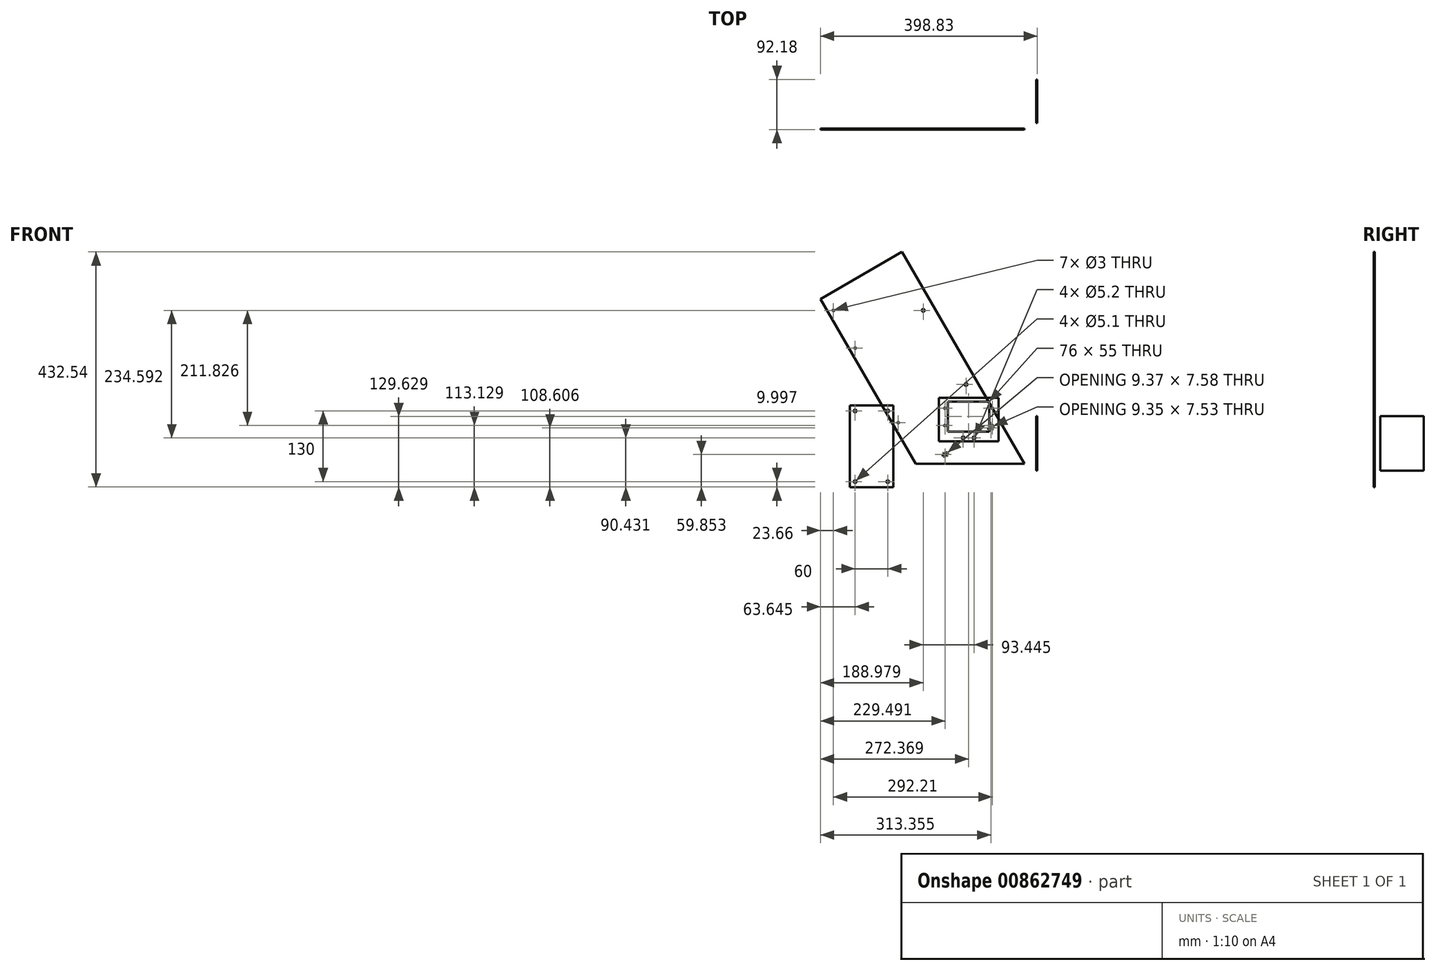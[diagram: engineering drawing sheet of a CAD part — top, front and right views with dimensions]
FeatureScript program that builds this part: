
annotation { "Feature Type Name" : "Feature", "Feature Type Description" : "" }
export const myFeature = defineFeature(function(context is Context, id is Id, definition is map)
    precondition{}
    {
        {
            var Q0;
            Q0=qCreatedBy(makeId("Front.planeOp"),FACE);
            var sketch = newSketch(context, id + "F0", { "sketchPlane" : qUnion([Q0])});
            skLineSegment(sketch, "E0", {"start": v(-221.83, -33.9) * mm, "end": v(-21.83, -33.9) * mm});
            skLineSegment(sketch, "E1", {"start": v(-21.83, -33.9) * mm, "end": v(-71.83, 52.7) * mm});
            skLineSegment(sketch, "E2", {"start": v(-71.83, 52.7) * mm, "end": v(-221.83, -33.9) * mm, "construction": true});
            skPoint(sketch, "E3", {"position": v(-150.09, -27.11) * mm});
            skLineSegment(sketch, "E4.bottom", {"start": v(-163.9, -17.83) * mm, "end": v(-168.23, -20.33) * mm});
            skLineSegment(sketch, "E4.top", {"start": v(-166.45, -13.4) * mm, "end": v(-170.78, -15.9) * mm});
            skLineSegment(sketch, "E4.left", {"start": v(-162.98, -14.41) * mm, "end": v(-163.03, -14.32) * mm});
            skLineSegment(sketch, "E4.right", {"start": v(-171.64, -19.41) * mm, "end": v(-171.7, -19.32) * mm});
            skPoint(sketch, "E4.middle", {"position": v(-167.34, -16.87) * mm});
            skPoint(sketch, "E5.visualSharp", {"position": v(-164.28, -12.16) * mm});
            skArc(sketch, "E5.filletArc", {"start": v(-163.03, -14.32) * mm, "mid": v(-164.55, -13.16) * mm, "end": v(-166.45, -13.4) * mm});
            skPoint(sketch, "E6.visualSharp", {"position": v(-161.73, -16.58) * mm});
            skArc(sketch, "E6.filletArc", {"start": v(-163.9, -17.83) * mm, "mid": v(-162.73, -16.3) * mm, "end": v(-162.98, -14.41) * mm});
            skPoint(sketch, "E7.visualSharp", {"position": v(-170.4, -21.58) * mm});
            skArc(sketch, "E7.filletArc", {"start": v(-171.64, -19.41) * mm, "mid": v(-170.13, -20.57) * mm, "end": v(-168.23, -20.33) * mm});
            skPoint(sketch, "E8.visualSharp", {"position": v(-172.94, -17.16) * mm});
            skArc(sketch, "E8.filletArc", {"start": v(-170.78, -15.9) * mm, "mid": v(-171.94, -17.43) * mm, "end": v(-171.7, -19.32) * mm});
            skLineSegment(sketch, "E9.bottom", {"start": v(-80.04, 30.95) * mm, "end": v(-84.38, 28.45) * mm});
            skLineSegment(sketch, "E9.top", {"start": v(-82.57, 35.33) * mm, "end": v(-86.9, 32.82) * mm});
            skLineSegment(sketch, "E9.left", {"start": v(-79.03, 34.17) * mm, "end": v(-79.05, 34.22) * mm});
            skLineSegment(sketch, "E9.right", {"start": v(-87.9, 29.56) * mm, "end": v(-87.92, 29.6) * mm});
            skPoint(sketch, "E9.middle", {"position": v(-82.9, 31.88) * mm});
            skArc(sketch, "E10.filletArc", {"start": v(-79.05, 34.22) * mm, "mid": v(-80.56, 35.55) * mm, "end": v(-82.57, 35.33) * mm});
            skArc(sketch, "E11.filletArc", {"start": v(-80.04, 30.95) * mm, "mid": v(-78.91, 32.36) * mm, "end": v(-79.03, 34.17) * mm});
            skArc(sketch, "E12.filletArc", {"start": v(-87.9, 29.56) * mm, "mid": v(-86.39, 28.23) * mm, "end": v(-84.38, 28.45) * mm});
            skArc(sketch, "E13.filletArc", {"start": v(-86.9, 32.82) * mm, "mid": v(-88.04, 31.4) * mm, "end": v(-87.92, 29.6) * mm});
            skLineSegment(sketch, "E14", {"start": v(-221.83, -33.9) * mm, "end": v(-396.83, 269.21) * mm});
            skLineSegment(sketch, "E15", {"start": v(-396.83, 269.21) * mm, "end": v(-246.83, 355.82) * mm});
            skLineSegment(sketch, "E16", {"start": v(-246.83, 355.82) * mm, "end": v(-71.83, 52.7) * mm});
            skCircle(sketch, "E17", {"center": v(-129.15, 112) * mm, "radius": 2.6 * mm});
            skCircle(sketch, "E18", {"center": v(-207.85, 248.3) * mm, "radius": 2.6 * mm});
            skCircle(sketch, "E19", {"center": v(-253.92, 41.69) * mm, "radius": 1.5 * mm});
            skCircle(sketch, "E20", {"center": v(-333.17, 178.95) * mm, "radius": 1.5 * mm});
            skCircle(sketch, "E21", {"center": v(-373.17, 248.23) * mm, "radius": 1.5 * mm});
            skSolve(sketch);
        }
        {
            var Q0;
            Q0 = qSketchRegion(id + "F0", true);
            extrude(context, id + "F1", {"entities" : qUnion([Q0]), "depth" : 2 * mm, "offsetDistance" : 25 * mm});
        }
        {
            var Q0;
            Q0=qCreatedBy(makeId("Right.planeOp"),FACE);
            var sketch = newSketch(context, id + "F2", { "sketchPlane" : qUnion([Q0])});
            skLineSegment(sketch, "E22.bottom", {"start": v(10.18, 53.74) * mm, "end": v(90.18, 53.74) * mm});
            skLineSegment(sketch, "E22.top", {"start": v(10.18, -46.26) * mm, "end": v(90.18, -46.26) * mm});
            skLineSegment(sketch, "E22.left", {"start": v(10.18, 53.74) * mm, "end": v(10.18, -46.26) * mm});
            skLineSegment(sketch, "E22.right", {"start": v(90.18, 53.74) * mm, "end": v(90.18, -46.26) * mm});
            skSolve(sketch);
        }
        {
            var Q0;
            Q0 = qSketchRegion(id + "F2", true);
            extrude(context, id + "F3", {"entities" : qUnion([Q0]), "depth" : 2 * mm, "offsetDistance" : 25 * mm});
        }
        {
            var Q0;
            Q0=qCreatedBy(makeId("Front.planeOp"),FACE);
            var sketch = newSketch(context, id + "F4", { "sketchPlane" : qUnion([Q0])});
            skLineSegment(sketch, "E23.bottom", {"start": v(-179.4, 87.36) * mm, "end": v(-69.4, 87.36) * mm});
            skLineSegment(sketch, "E23.top", {"start": v(-179.4, 7.36) * mm, "end": v(-69.4, 7.36) * mm});
            skLineSegment(sketch, "E23.left", {"start": v(-179.4, 87.36) * mm, "end": v(-179.4, 7.36) * mm});
            skLineSegment(sketch, "E23.right", {"start": v(-69.4, 87.36) * mm, "end": v(-69.4, 7.36) * mm});
            skLineSegment(sketch, "E24.bottom", {"start": v(-162.46, 80.4) * mm, "end": v(-86.46, 80.4) * mm});
            skLineSegment(sketch, "E24.top", {"start": v(-162.46, 25.4) * mm, "end": v(-86.46, 25.4) * mm});
            skLineSegment(sketch, "E24.left", {"start": v(-162.46, 80.4) * mm, "end": v(-162.46, 25.4) * mm});
            skLineSegment(sketch, "E24.right", {"start": v(-86.46, 80.4) * mm, "end": v(-86.46, 25.4) * mm});
            skCircle(sketch, "E25", {"center": v(-80.96, 68.4) * mm, "radius": 1.5 * mm});
            skCircle(sketch, "E26", {"center": v(-80.96, 36.4) * mm, "radius": 1.5 * mm});
            skCircle(sketch, "E27", {"center": v(-134.4, 13.71) * mm, "radius": 2.6 * mm});
            skCircle(sketch, "E28", {"center": v(-114.4, 13.71) * mm, "radius": 2.6 * mm});
            skCircle(sketch, "E29", {"center": v(-167.96, 68.4) * mm, "radius": 1.5 * mm});
            skCircle(sketch, "E30", {"center": v(-167.96, 36.4) * mm, "radius": 1.5 * mm});
            skSolve(sketch);
        }
        {
            var Q0;
            Q0=makeQuery(id+"F4.imprint","IMPRINT",FACE,{"disambiguationData":[TD([[makeQuery(id+"F4.imprint","IMPRINT",EDGE,{"derivedFrom":sQuery(id+"F4.wireOp",EDGE,"E23.bottom")}),-1.0]])]});
            extrude(context, id + "F5", {"entities" : qUnion([Q0]), "depth" : 2 * mm, "offsetDistance" : 25 * mm});
        }
        {
            var Q0;
            Q0=qCreatedBy(makeId("Front.planeOp"),FACE);
            var sketch = newSketch(context, id + "F6", { "sketchPlane" : qUnion([Q0])});
            skLineSegment(sketch, "E31.bottom", {"start": v(-343.19, 73.28) * mm, "end": v(-263.19, 73.28) * mm});
            skLineSegment(sketch, "E31.top", {"start": v(-343.19, -76.72) * mm, "end": v(-263.19, -76.72) * mm});
            skLineSegment(sketch, "E31.left", {"start": v(-343.19, 73.28) * mm, "end": v(-343.19, -76.72) * mm});
            skLineSegment(sketch, "E31.right", {"start": v(-263.19, 73.28) * mm, "end": v(-263.19, -76.72) * mm});
            skCircle(sketch, "E32", {"center": v(-333.19, 63.28) * mm, "radius": 2.55 * mm});
            skCircle(sketch, "E33", {"center": v(-273.19, 63.28) * mm, "radius": 2.55 * mm});
            skCircle(sketch, "E34", {"center": v(-333.19, -66.72) * mm, "radius": 2.55 * mm});
            skCircle(sketch, "E35", {"center": v(-273.19, -66.72) * mm, "radius": 2.55 * mm});
            skSolve(sketch);
        }
        {
            var Q0;
            Q0=makeQuery(id+"F6.imprint","IMPRINT",FACE,{"disambiguationData":[TD([[makeQuery(id+"F6.imprint","IMPRINT",EDGE,{"derivedFrom":sQuery(id+"F6.wireOp",EDGE,"E31.bottom")}),-1.0]])]});
            extrude(context, id + "F7", {"entities" : qUnion([Q0]), "depth" : 2 * mm, "offsetDistance" : 25 * mm});
        }
    });
